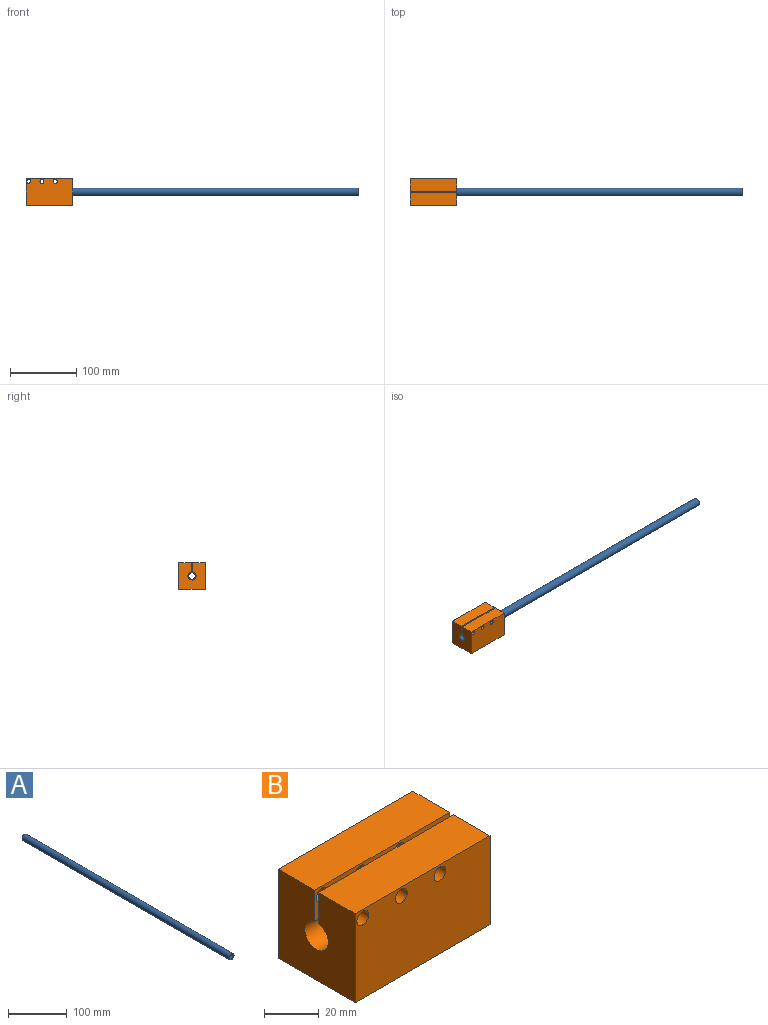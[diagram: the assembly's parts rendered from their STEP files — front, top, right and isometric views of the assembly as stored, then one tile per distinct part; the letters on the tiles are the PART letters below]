
ASSEMBLY  parts=2 mates=1
PART A: 4 faces, bbox 12x500x12 mm
  f0: cylinder r=5mm len=500mm, axis (0,1,0), area 15708mm2, adj f2,f3
  f1: cylinder r=6mm len=500mm, axis (0,1,0), area 18849.6mm2, adj f2,f3
  f2: plane 12x12mm, normal (0,-1,0), area 34.6mm2, adj f0,f1
  f3: plane 12x12mm, normal (0,1,0), area 34.6mm2, adj f0,f1
PART B: 16 faces, bbox 70x40x40 mm
  f0: plane 70x19mm, normal (0,0,1), area 1330mm2, adj f1,f2,f3,f8
  f1: plane 40x40mm, normal (-1,0,0), area 1457.1mm2, adj f0,f3,f4,f5,f6,f7,f8,f9
  f2: plane 40x40mm, normal (1,0,0), area 1457.1mm2, adj f0,f3,f4,f5,f6,f7,f8,f9
  f3: plane 70x40mm, normal (0,-1,0), area 2712.3mm2, adj f0,f1,f2,f6,f13,f14,f15
  f4: plane 70x40mm, normal (0,1,0), area 2712.3mm2, adj f1,f2,f5,f6,f10,f11,f12
  f5: plane 70x19mm, normal (0,0,1), area 1330mm2, adj f1,f2,f4,f9
  f6: plane 70x40mm, normal (0,0,-1), area 2800mm2, adj f1,f2,f3,f4
  f7: cylinder r=6.05mm len=70mm, axis (-1,0,0), area 2520.3mm2, adj f1,f2,f8,f9
  f8: plane 70x14.03mm, normal (0,1,0), area 894.7mm2, adj f0,f1,f2,f7,f13,f14,f15
  f9: plane 70x14.03mm, normal (0,-1,0), area 894.7mm2, adj f1,f2,f5,f7,f10,f11,f12
  f10: cylinder r=3.05mm len=19mm, axis (0,-1,0), area 364.1mm2, adj f4,f9
  f11: cylinder r=3.05mm len=19mm, axis (0,-1,0), area 364.1mm2, adj f4,f9
  f12: cylinder r=3.05mm len=19mm, axis (0,-1,0), area 364.1mm2, adj f4,f9
  f13: cylinder r=3.05mm len=19mm, axis (0,-1,0), area 364.1mm2, adj f3,f8
  f14: cylinder r=3.05mm len=19mm, axis (0,-1,0), area 364.1mm2, adj f3,f8
  f15: cylinder r=3.05mm len=19mm, axis (0,-1,0), area 364.1mm2, adj f3,f8
PLACE A rot(axis=(-0.11,0.11,0.99),90.7deg) t=(-0.03,20,20)mm
PLACE B at identity
MATE cylindrical A.f1 <-> B.f7  axis (-1,0,0) through (249.97,20,20)mm
